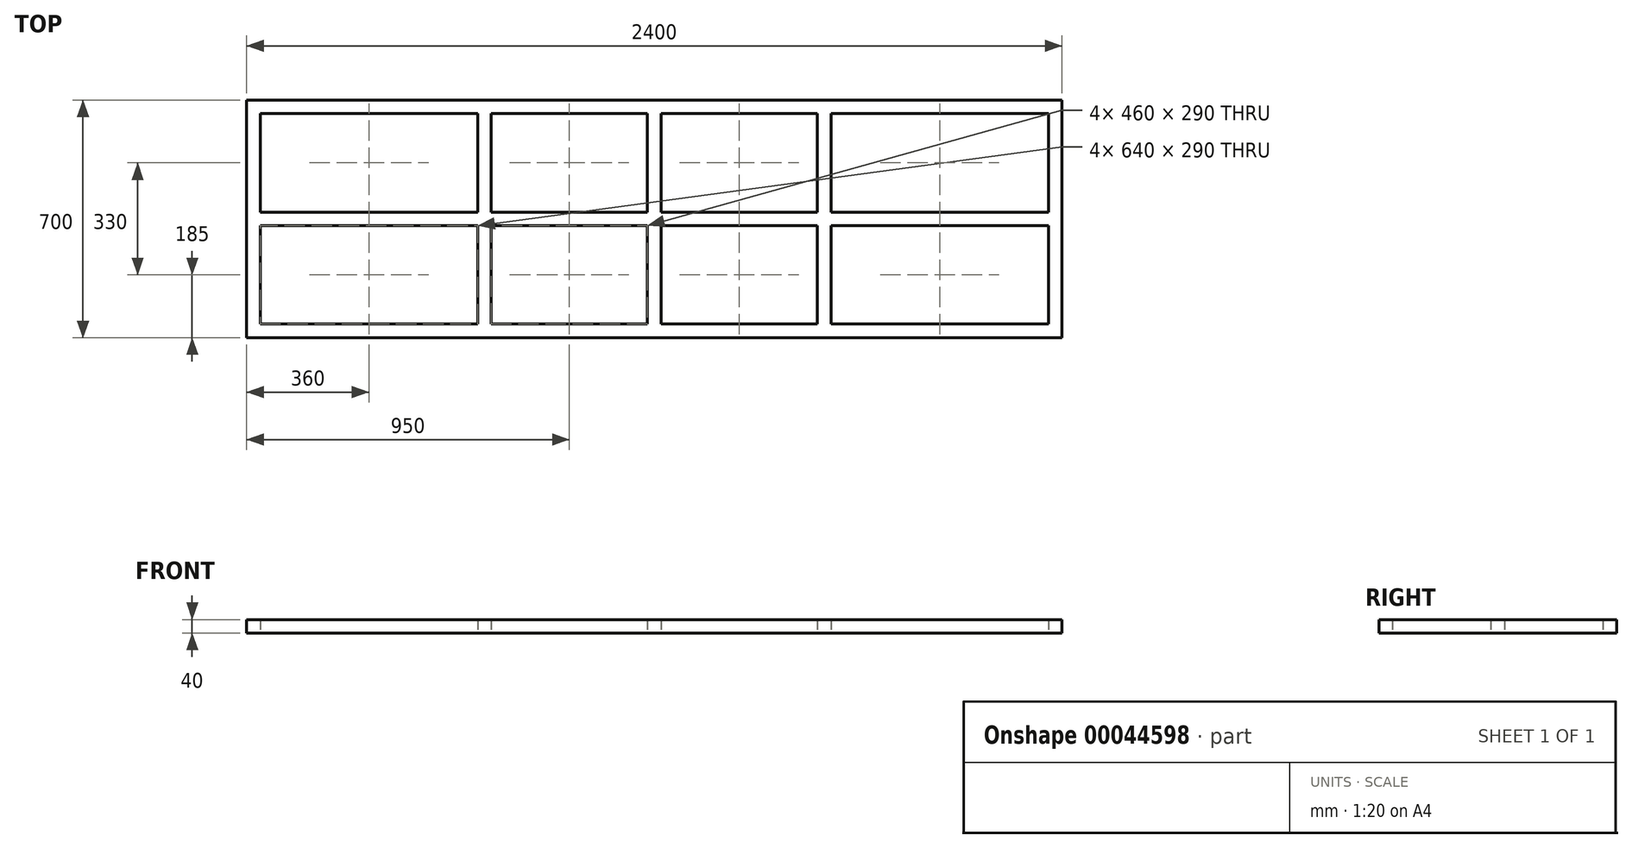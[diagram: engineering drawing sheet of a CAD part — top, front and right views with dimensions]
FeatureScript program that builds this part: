
annotation { "Feature Type Name" : "Feature", "Feature Type Description" : "" }
export const myFeature = defineFeature(function(context is Context, id is Id, definition is map)
    precondition{}
    {
        {
            var Q0;
            Q0=qCreatedBy(makeId("Top.planeOp"),FACE);
            var sketch = newSketch(context, id + "F0", { "sketchPlane" : qUnion([Q0])});
            skLineSegment(sketch, "E0.rect.bottom", {"start": v(1200, 350) * mm, "end": v(-1200, 350) * mm});
            skLineSegment(sketch, "E0.rect.top", {"start": v(1200, -350) * mm, "end": v(-1200, -350) * mm});
            skLineSegment(sketch, "E0.rect.left", {"start": v(1200, 350) * mm, "end": v(1200, -350) * mm});
            skLineSegment(sketch, "E0.rect.right", {"start": v(-1200, 350) * mm, "end": v(-1200, -350) * mm});
            skPoint(sketch, "E0.rect.middle", {"position": v(0, 0) * mm});
            skLineSegment(sketch, "E1.rect.bottom", {"start": v(-1160, 310) * mm, "end": v(1160, 310) * mm});
            skLineSegment(sketch, "E1.rect.top", {"start": v(-1160, -310) * mm, "end": v(1160, -310) * mm});
            skLineSegment(sketch, "E1.rect.left", {"start": v(-1160, 310) * mm, "end": v(-1160, -310) * mm});
            skLineSegment(sketch, "E1.rect.right", {"start": v(1160, 310) * mm, "end": v(1160, -310) * mm});
            skLineSegment(sketch, "E2", {"start": v(-20, 310) * mm, "end": v(-20, -310) * mm});
            skLineSegment(sketch, "E3", {"start": v(0, 0) * mm, "end": v(0, 310) * mm, "construction": true});
            skLineSegment(sketch, "E4", {"start": v(20, 310) * mm, "end": v(20, -310) * mm});
            skLineSegment(sketch, "E5", {"start": v(-1160, 0) * mm, "end": v(1160, 0) * mm, "construction": true});
            skLineSegment(sketch, "E6", {"start": v(-1160, 20) * mm, "end": v(1160, 20) * mm});
            skLineSegment(sketch, "E7", {"start": v(-1160, -20) * mm, "end": v(1160, -20) * mm});
            skLineSegment(sketch, "E8", {"start": v(-520, 310) * mm, "end": v(-520, -310) * mm});
            skLineSegment(sketch, "E9", {"start": v(-480, 310) * mm, "end": v(-480, -310) * mm});
            skLineSegment(sketch, "E10", {"start": v(480, 310) * mm, "end": v(480, -310) * mm});
            skLineSegment(sketch, "E11", {"start": v(520, 310) * mm, "end": v(520, -310) * mm});
            skSolve(sketch);
        }
        {
            var Q0;
            Q0=makeQuery(id+"F0.imprint","IMPRINT",FACE,{"disambiguationData":[TD([[makeQuery(id+"F0.imprint","IMPRINT",EDGE,{"derivedFrom":sQuery(id+"F0.wireOp",EDGE,"E0.rect.bottom")}),1.0]])]});
            var Q1;
            {var subQ3=sQuery(id+"F0.wireOp",EDGE,"E6");var subQ5=sQuery(id+"F0.wireOp",EDGE,"E1.rect.left");var subQ6=makeQuery(id+"F0.imprint","INTERSECT",VERTEX,{"derivedFrom":[subQ5,subQ3]});Q1=makeQuery(id+"F0.imprint","IMPRINT",FACE,{"disambiguationData":[TD([[makeQuery(id+"F0.imprint","IMPRINT",EDGE,{"disambiguationData":[TD([[subQ6,-1.0]])],"derivedFrom":subQ5}),1.0]])]});}
            var Q2;
            {var subQ0=sQuery(id+"F0.wireOp",EDGE,"E8");var subQ3=sQuery(id+"F0.wireOp",EDGE,"E6");var subQ4=makeQuery(id+"F0.imprint","INTERSECT",VERTEX,{"derivedFrom":[subQ3,subQ0]});Q2=makeQuery(id+"F0.imprint","IMPRINT",FACE,{"disambiguationData":[TD([[makeQuery(id+"F0.imprint","IMPRINT",EDGE,{"disambiguationData":[TD([[subQ4,-1.0]])],"derivedFrom":subQ3}),-1.0]])]});}
            var Q3;
            {var subQ0=sQuery(id+"F0.wireOp",EDGE,"E8");var subQ3=sQuery(id+"F0.wireOp",EDGE,"E1.rect.bottom");var subQ4=makeQuery(id+"F0.imprint","INTERSECT",VERTEX,{"derivedFrom":[subQ3,subQ0]});Q3=makeQuery(id+"F0.imprint","IMPRINT",FACE,{"disambiguationData":[TD([[makeQuery(id+"F0.imprint","IMPRINT",EDGE,{"disambiguationData":[TD([[subQ4,-1.0]])],"derivedFrom":subQ3}),-1.0]])]});}
            var Q4;
            {var subQ3=sQuery(id+"F0.wireOp",EDGE,"E1.rect.top");var subQ5=sQuery(id+"F0.wireOp",EDGE,"E8");var subQ7=makeQuery(id+"F0.imprint","INTERSECT",VERTEX,{"derivedFrom":[subQ3,subQ5]});Q4=makeQuery(id+"F0.imprint","IMPRINT",FACE,{"disambiguationData":[TD([[makeQuery(id+"F0.imprint","IMPRINT",EDGE,{"disambiguationData":[TD([[subQ7,-1.0]])],"derivedFrom":subQ3}),1.0]])]});}
            var Q5;
            {var subQ3=sQuery(id+"F0.wireOp",EDGE,"E6");var subQ5=sQuery(id+"F0.wireOp",EDGE,"E2");var subQ7=makeQuery(id+"F0.imprint","INTERSECT",VERTEX,{"derivedFrom":[subQ5,subQ3]});Q5=makeQuery(id+"F0.imprint","IMPRINT",FACE,{"disambiguationData":[TD([[makeQuery(id+"F0.imprint","IMPRINT",EDGE,{"disambiguationData":[TD([[subQ7,-1.0]])],"derivedFrom":subQ5}),-1.0]])]});}
            var Q6;
            {var subQ3=sQuery(id+"F0.wireOp",EDGE,"E2");var subQ5=sQuery(id+"F0.wireOp",EDGE,"E1.rect.bottom");var subQ7=makeQuery(id+"F0.imprint","INTERSECT",VERTEX,{"derivedFrom":[subQ5,subQ3]});Q6=makeQuery(id+"F0.imprint","IMPRINT",FACE,{"disambiguationData":[TD([[makeQuery(id+"F0.imprint","IMPRINT",EDGE,{"disambiguationData":[TD([[subQ7,-1.0]])],"derivedFrom":subQ5}),-1.0]])]});}
            var Q7;
            {var subQ3=sQuery(id+"F0.wireOp",EDGE,"E2");var subQ5=sQuery(id+"F0.wireOp",EDGE,"E1.rect.top");var subQ6=makeQuery(id+"F0.imprint","INTERSECT",VERTEX,{"derivedFrom":[subQ5,subQ3]});Q7=makeQuery(id+"F0.imprint","IMPRINT",FACE,{"disambiguationData":[TD([[makeQuery(id+"F0.imprint","IMPRINT",EDGE,{"disambiguationData":[TD([[subQ6,-1.0]])],"derivedFrom":subQ5}),1.0]])]});}
            var Q8;
            {var subQ3=sQuery(id+"F0.wireOp",EDGE,"E1.rect.bottom");var subQ5=sQuery(id+"F0.wireOp",EDGE,"E10");var subQ7=makeQuery(id+"F0.imprint","INTERSECT",VERTEX,{"derivedFrom":[subQ3,subQ5]});Q8=makeQuery(id+"F0.imprint","IMPRINT",FACE,{"disambiguationData":[TD([[makeQuery(id+"F0.imprint","IMPRINT",EDGE,{"disambiguationData":[TD([[subQ7,-1.0]])],"derivedFrom":subQ3}),-1.0]])]});}
            var Q9;
            {var subQ0=sQuery(id+"F0.wireOp",EDGE,"E10");var subQ3=sQuery(id+"F0.wireOp",EDGE,"E1.rect.top");var subQ4=makeQuery(id+"F0.imprint","INTERSECT",VERTEX,{"derivedFrom":[subQ3,subQ0]});Q9=makeQuery(id+"F0.imprint","IMPRINT",FACE,{"disambiguationData":[TD([[makeQuery(id+"F0.imprint","IMPRINT",EDGE,{"disambiguationData":[TD([[subQ4,-1.0]])],"derivedFrom":subQ3}),1.0]])]});}
            var Q10;
            {var subQ3=sQuery(id+"F0.wireOp",EDGE,"E6");var subQ5=sQuery(id+"F0.wireOp",EDGE,"E1.rect.right");var subQ7=makeQuery(id+"F0.imprint","INTERSECT",VERTEX,{"derivedFrom":[subQ5,subQ3]});Q10=makeQuery(id+"F0.imprint","IMPRINT",FACE,{"disambiguationData":[TD([[makeQuery(id+"F0.imprint","IMPRINT",EDGE,{"disambiguationData":[TD([[subQ7,-1.0]])],"derivedFrom":subQ5}),-1.0]])]});}
            var Q11;
            {var subQ3=sQuery(id+"F0.wireOp",EDGE,"E4");var subQ5=sQuery(id+"F0.wireOp",EDGE,"E6");var subQ7=makeQuery(id+"F0.imprint","INTERSECT",VERTEX,{"derivedFrom":[subQ3,subQ5]});Q11=makeQuery(id+"F0.imprint","IMPRINT",FACE,{"disambiguationData":[TD([[makeQuery(id+"F0.imprint","IMPRINT",EDGE,{"disambiguationData":[TD([[subQ7,-1.0]])],"derivedFrom":subQ3}),1.0]])]});}
            var Q12;
            {var subQ3=sQuery(id+"F0.wireOp",EDGE,"E6");var subQ5=sQuery(id+"F0.wireOp",EDGE,"E10");var subQ7=makeQuery(id+"F0.imprint","INTERSECT",VERTEX,{"derivedFrom":[subQ3,subQ5]});Q12=makeQuery(id+"F0.imprint","IMPRINT",FACE,{"disambiguationData":[TD([[makeQuery(id+"F0.imprint","IMPRINT",EDGE,{"disambiguationData":[TD([[subQ7,-1.0]])],"derivedFrom":subQ3}),-1.0]])]});}
            var Q13;
            {var subQ0=sQuery(id+"F0.wireOp",EDGE,"E6");var subQ3=sQuery(id+"F0.wireOp",EDGE,"E2");var subQ4=makeQuery(id+"F0.imprint","INTERSECT",VERTEX,{"derivedFrom":[subQ3,subQ0]});Q13=makeQuery(id+"F0.imprint","IMPRINT",FACE,{"disambiguationData":[TD([[makeQuery(id+"F0.imprint","IMPRINT",EDGE,{"disambiguationData":[TD([[subQ4,-1.0]])],"derivedFrom":subQ3}),1.0]])]});}
            extrude(context, id + "F1", {"entities" : qUnion([Q0, Q1, Q2, Q3, Q4, Q5, Q6, Q7, Q8, Q9, Q10, Q11, Q12, Q13]), "depth" : 40 * mm});
        }
    });
